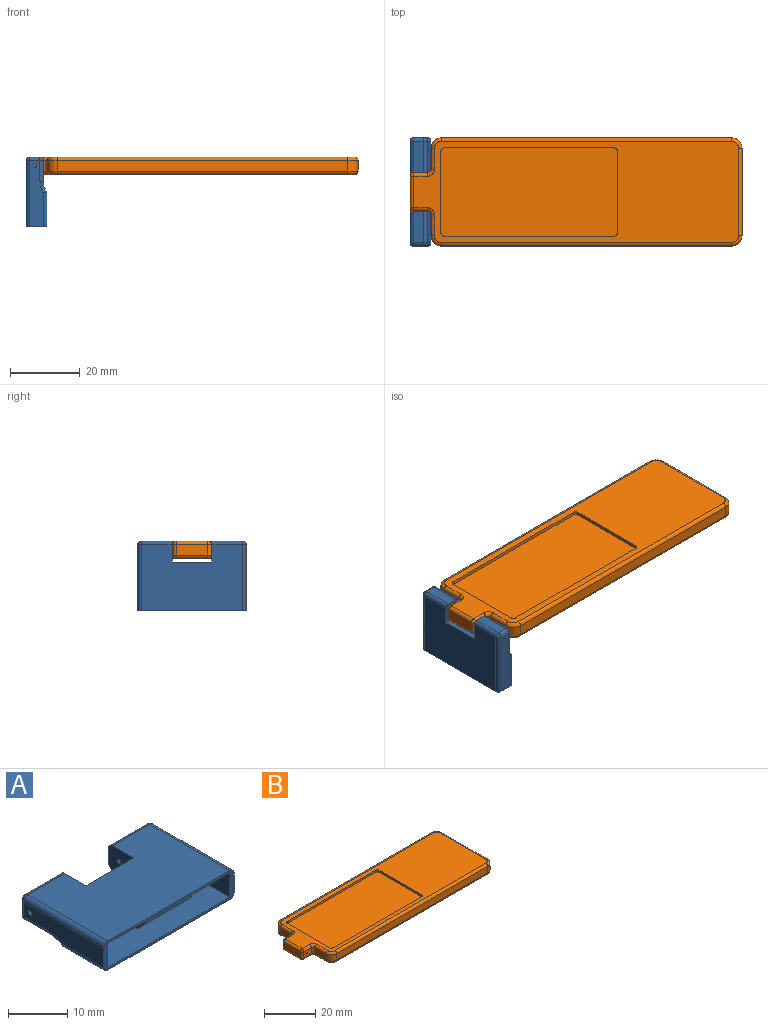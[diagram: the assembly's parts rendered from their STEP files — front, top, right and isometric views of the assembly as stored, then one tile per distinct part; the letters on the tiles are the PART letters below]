
ASSEMBLY  parts=2 mates=1
PART A: 42 faces, bbox 31x20x6 mm
  f0: plane 29x9.5mm, normal (0,0,-1), area 237mm2, adj f1,f13,f15,f16,f37,f38,f39
  f1: plane 31x6mm, normal (0,-1,0), area 45.6mm2, adj f0,f4,f5,f10,f11,f13,f14,f15
  f2: plane 29x6mm, normal (0,0,-1), area 117mm2, adj f7,f8,f9,f12,f21,f24,f29,f32
  f3: plane 8.8x3mm, normal (0,1,0), area 26.4mm2, adj f9,f26,f29,f30
  f4: plane 19x4mm, normal (-1,0,0), area 67.2mm2, adj f1,f27,f30,f32,f33,f34,f35
  f5: plane 19x4mm, normal (1,0,0), area 67.2mm2, adj f1,f17,f20,f23,f24,f25,f36
  f6: plane 8.8x3mm, normal (0,1,0), area 26.4mm2, adj f7,f18,f20,f21
  f7: plane 6x5mm, normal (-1,0,0), area 29.1mm2, adj f2,f6,f8,f10,f18,f21,f36
  f8: plane 11.4x5mm, normal (0,1,0), area 57mm2, adj f2,f7,f9,f10
  f9: plane 6x5mm, normal (1,0,0), area 29.1mm2, adj f2,f3,f8,f10,f26,f29,f35
  f10: plane 29x19mm, normal (0,0,1), area 494mm2, adj f1,f7,f8,f9,f17,f18,f26,f27
  f11: plane 29x10mm, normal (0,0,-1), area 290mm2, adj f1,f12,f23,f33
  f12: cylinder r=5mm len=29mm, axis (1,0,0), area 93.3mm2, adj f2,f11,f25,f34
  f13: plane 9.5x5mm, normal (1,0,0), area 47.5mm2, adj f0,f1,f14,f16
  f14: plane 29x9.5mm, normal (0,0,1), area 275.5mm2, adj f1,f13,f15,f16
  f15: plane 9.5x5mm, normal (-1,0,0), area 47.5mm2, adj f0,f1,f14,f16
  f16: plane 29x5mm, normal (0,-1,0), area 145mm2, adj f0,f13,f14,f15
  f17: cylinder r=1mm len=19mm, axis (0,-1,0), area 29.8mm2, adj f1,f5,f10,f19
  f18: cylinder r=1mm len=8.8mm, axis (1,0,0), area 13.8mm2, adj f6,f7,f10,f19
  f19: sphere r=1mm, area 1.6mm2, adj f17,f18,f20
  f20: cylinder r=1mm len=3mm, axis (0,0,-1), area 4.7mm2, adj f5,f6,f19,f22
  f21: cylinder r=1mm len=8.8mm, axis (-1,0,0), area 13.8mm2, adj f2,f6,f7,f22
  f22: sphere r=1mm, area 1.6mm2, adj f20,f21,f24
  f23: cylinder r=1mm len=10mm, axis (0,-1,0), area 15.5mm2, adj f1,f5,f11,f25
  f24: cylinder r=1mm len=6mm, axis (0,1,0), area 9.4mm2, adj f2,f5,f22,f25
  f25: torus R=6mm, axis (1,0,0), area 5.2mm2, adj f5,f12,f23,f24
  f26: cylinder r=1mm len=8.8mm, axis (1,0,0), area 13.8mm2, adj f3,f9,f10,f28
  f27: cylinder r=1mm len=19mm, axis (0,1,0), area 29.8mm2, adj f1,f4,f10,f28
  f28: sphere r=1mm, area 1.6mm2, adj f26,f27,f30
  f29: cylinder r=1mm len=8.8mm, axis (-1,0,0), area 13.8mm2, adj f2,f3,f9,f31
  f30: cylinder r=1mm len=3mm, axis (0,0,1), area 4.7mm2, adj f3,f4,f28,f31
  f31: sphere r=1mm, area 1.6mm2, adj f29,f30,f32
  f32: cylinder r=1mm len=6mm, axis (0,-1,0), area 9.4mm2, adj f2,f4,f31,f34
  f33: cylinder r=1mm len=10mm, axis (0,1,0), area 15.5mm2, adj f1,f4,f11,f34
  f34: torus R=6mm, axis (1,0,0), area 5.2mm2, adj f4,f12,f32,f33
  f35: cylinder r=0.4mm len=9.8mm, axis (-1,0,0), area 24.6mm2, adj f4,f9
  f36: cylinder r=0.4mm len=9.8mm, axis (-1,0,0), area 24.6mm2, adj f5,f7
  f37: plane 3.5x2.5mm, normal (1,0,0), area 6.7mm2, adj f0,f1,f39,f40,f41
  f38: plane 3.5x2.5mm, normal (-1,0,0), area 6.7mm2, adj f0,f1,f39,f40,f41
  f39: plane 11x2.5mm, normal (0,1,0), area 27.5mm2, adj f0,f37,f38,f40
  f40: plane 11x1.5mm, normal (0,0,-1), area 16.5mm2, adj f37,f38,f39,f41
  f41: plane 11x2mm, normal (0,-0.71,-0.71), area 31.1mm2, adj f1,f37,f38,f40
PART B: 60 faces, bbox 95.2x31.5x5 mm
  f0: plane 93x29mm, normal (0,0,1), area 1301mm2, adj f17,f34,f36,f38,f40,f41,f42,f43
  f1: plane 83x3mm, normal (0,1,0), area 249mm2, adj f10,f13,f25,f49
  f2: plane 6x3mm, normal (-1,0,0), area 18mm2, adj f10,f14,f29,f45
  f3: plane 4x3mm, normal (0,1,0), area 11.5mm2, adj f14,f33,f37,f41,f59
  f4: plane 9x3mm, normal (-1,0,0), area 27mm2, adj f16,f17,f30,f37
  f5: plane 4x3mm, normal (0,-1,0), area 11.5mm2, adj f15,f26,f30,f34,f59
  f6: plane 6x3mm, normal (-1,0,0), area 18mm2, adj f11,f15,f22,f38
  f7: plane 83x3mm, normal (0,-1,0), area 249mm2, adj f11,f12,f18,f42
  f8: plane 25x3mm, normal (1,0,0), area 75mm2, adj f12,f13,f21,f46
  f9: plane 93x29mm, normal (0,0,-1), area 2575.3mm2, adj f16,f18,f19,f20,f21,f22,f23,f24
  f10: cylinder r=3mm len=3mm, axis (0,0,1), area 14.1mm2, adj f1,f2,f27,f47
  f11: cylinder r=3mm len=3mm, axis (0,0,-1), area 14.1mm2, adj f6,f7,f20,f40
  f12: cylinder r=3mm len=3mm, axis (0,0,1), area 14.1mm2, adj f7,f8,f19,f44
  f13: cylinder r=3mm len=3mm, axis (0,0,-1), area 14.1mm2, adj f1,f8,f23,f48
  f14: cylinder r=1mm len=3mm, axis (0,0,1), area 4.7mm2, adj f2,f3,f31,f43
  f15: cylinder r=1mm len=3mm, axis (0,0,-1), area 4.7mm2, adj f5,f6,f24,f36
  f16: cylinder r=1mm len=9mm, axis (0,-1,0), area 14.1mm2, adj f4,f9,f28,f35
  f17: cylinder r=1mm len=9mm, axis (0,1,0), area 14.1mm2, adj f0,f4,f32,f39
  f18: cylinder r=1mm len=83mm, axis (1,0,0), area 130.4mm2, adj f7,f9,f19,f20
  f19: torus R=2mm, axis (0,0,1), area 6.5mm2, adj f9,f12,f18,f21
  f20: torus R=2mm, axis (0,0,1), area 6.5mm2, adj f9,f11,f18,f22
  f21: cylinder r=1mm len=25mm, axis (0,1,0), area 39.3mm2, adj f8,f9,f19,f23
  f22: cylinder r=1mm len=6mm, axis (0,-1,0), area 9.4mm2, adj f6,f9,f20,f24
  f23: torus R=2mm, axis (0,0,1), area 6.5mm2, adj f9,f13,f21,f25
  f24: torus R=2mm, axis (0,0,1), area 3.4mm2, adj f9,f15,f22,f26
  f25: cylinder r=1mm len=83mm, axis (-1,0,0), area 130.4mm2, adj f1,f9,f23,f27
  f26: cylinder r=1mm len=4mm, axis (1,0,0), area 6.3mm2, adj f5,f9,f24,f28
  f27: torus R=2mm, axis (0,0,1), area 6.5mm2, adj f9,f10,f25,f29
  f28: sphere r=1mm, area 1.6mm2, adj f16,f26,f30
  f29: cylinder r=1mm len=6mm, axis (0,-1,0), area 9.4mm2, adj f2,f9,f27,f31
  f30: cylinder r=1mm len=3mm, axis (0,0,1), area 4.7mm2, adj f4,f5,f28,f32
  f31: torus R=2mm, axis (0,0,1), area 3.4mm2, adj f9,f14,f29,f33
  f32: sphere r=1mm, area 1.6mm2, adj f17,f30,f34
  f33: cylinder r=1mm len=4mm, axis (-1,0,0), area 6.3mm2, adj f3,f9,f31,f35
  f34: cylinder r=1mm len=4mm, axis (-1,0,0), area 6.3mm2, adj f0,f5,f32,f36
  f35: sphere r=1mm, area 1.6mm2, adj f16,f33,f37
  f36: torus R=2mm, axis (0,0,1), area 3.4mm2, adj f0,f15,f34,f38
  f37: cylinder r=1mm len=3mm, axis (0,0,-1), area 4.7mm2, adj f3,f4,f35,f39
  f38: cylinder r=1mm len=6mm, axis (0,1,0), area 9.4mm2, adj f0,f6,f36,f40
  f39: sphere r=1mm, area 1.6mm2, adj f17,f37,f41
  f40: torus R=2mm, axis (0,0,1), area 6.5mm2, adj f0,f11,f38,f42
  f41: cylinder r=1mm len=4mm, axis (1,0,0), area 6.3mm2, adj f0,f3,f39,f43
  f42: cylinder r=1mm len=83mm, axis (-1,0,0), area 130.4mm2, adj f0,f7,f40,f44
  f43: torus R=2mm, axis (0,0,1), area 3.4mm2, adj f0,f14,f41,f45
  f44: torus R=2mm, axis (0,0,1), area 6.5mm2, adj f0,f12,f42,f46
  f45: cylinder r=1mm len=6mm, axis (0,1,0), area 9.4mm2, adj f0,f2,f43,f47
  f46: cylinder r=1mm len=25mm, axis (0,-1,0), area 39.3mm2, adj f0,f8,f44,f48
  f47: torus R=2mm, axis (0,0,1), area 6.5mm2, adj f0,f10,f45,f49
  f48: torus R=2mm, axis (0,0,1), area 6.5mm2, adj f0,f13,f46,f49
  f49: cylinder r=1mm len=83mm, axis (1,0,0), area 130.4mm2, adj f0,f1,f47,f48
  f50: plane 48.5x1mm, normal (0,-1,0), area 48.5mm2, adj f0,f51,f57,f58
  f51: cylinder r=1mm len=1mm, axis (0,0,1), area 1.6mm2, adj f0,f50,f52,f58
  f52: plane 23.25x1mm, normal (1,0,0), area 23.2mm2, adj f0,f51,f53,f58
  f53: cylinder r=1mm len=1mm, axis (0,0,1), area 1.6mm2, adj f0,f52,f54,f58
  f54: plane 48.5x1mm, normal (0,1,0), area 48.5mm2, adj f0,f53,f55,f58
  f55: cylinder r=1mm len=1mm, axis (0,0,1), area 1.6mm2, adj f0,f54,f56,f58
  f56: plane 23.25x1mm, normal (-1,0,0), area 23.2mm2, adj f0,f55,f57,f58
  f57: cylinder r=1mm len=1mm, axis (0,0,1), area 1.6mm2, adj f0,f50,f56,f58
  f58: plane 50.5x25.25mm, normal (0,0,1), area 1274.3mm2, adj f50,f51,f52,f53,f54,f55,f56,f57
  f59: cylinder r=0.4mm len=11mm, axis (0,1,0), area 27.6mm2, adj f3,f5
PLACE A rot(axis=(0.58,-0.58,-0.58),120deg) t=(-1,0,5)mm
PLACE B at identity
MATE fastened A.f35 <-> B.f59  axis (0,-1,0) through (-3.5,-9.8,2.5)mm
